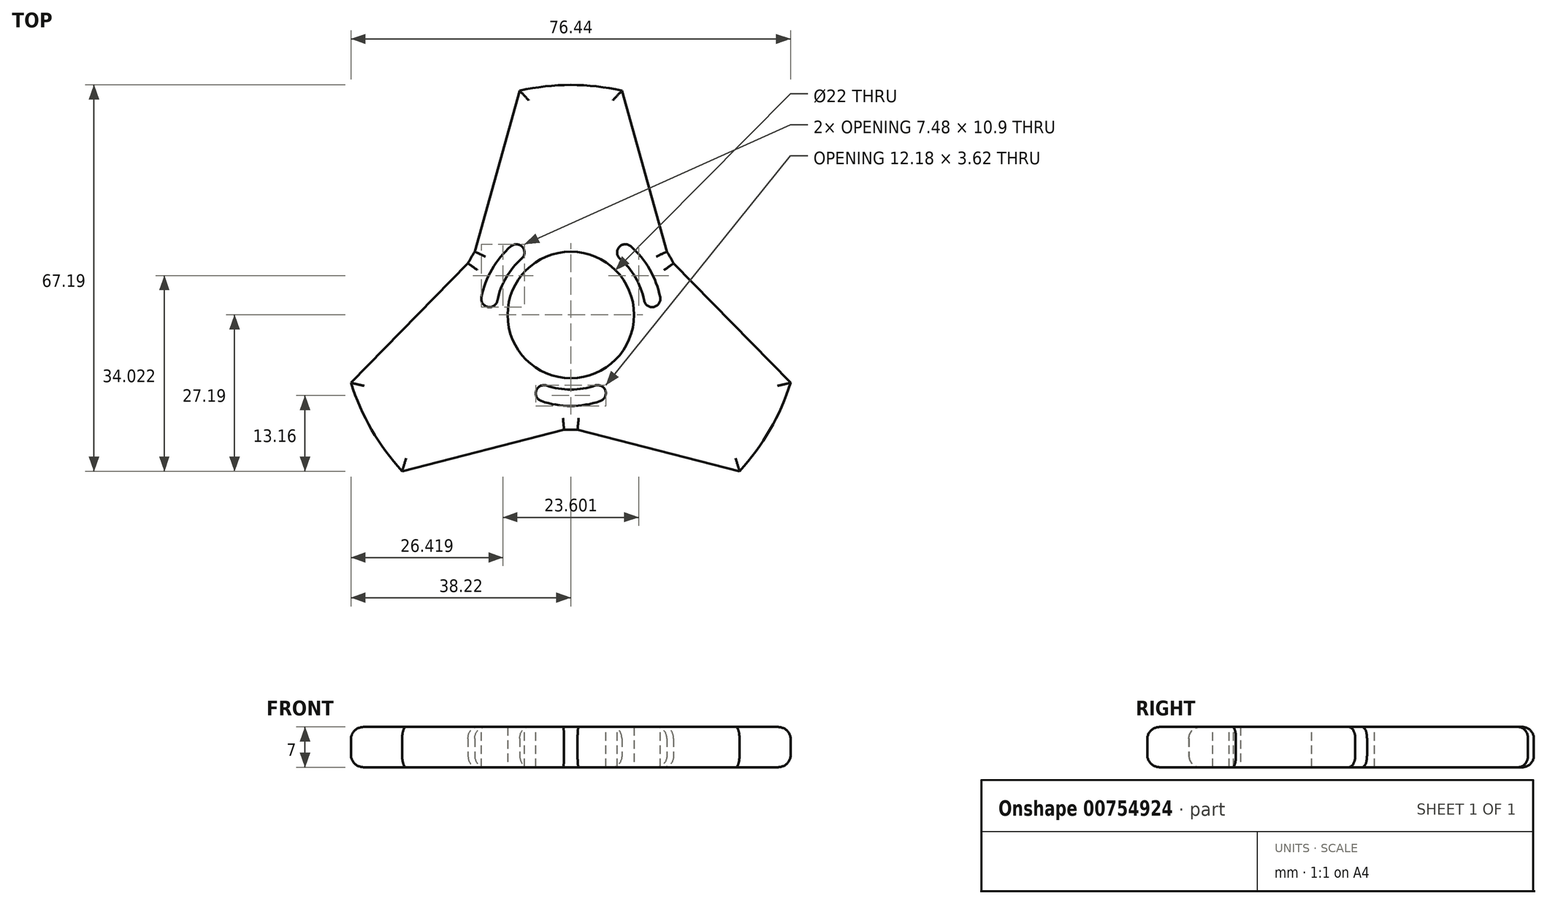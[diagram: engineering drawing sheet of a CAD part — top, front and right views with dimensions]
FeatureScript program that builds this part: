
annotation { "Feature Type Name" : "Feature", "Feature Type Description" : "" }
export const myFeature = defineFeature(function(context is Context, id is Id, definition is map)
    precondition{}
    {
        {
            var Q0;
            Q0=qCreatedBy(makeId("Top.planeOp"),FACE);
            var sketch = newSketch(context, id + "F0", { "sketchPlane" : qUnion([Q0])});
            skCircle(sketch, "E0", {"center": v(0, 0) * mm, "radius": 11 * mm});
            skLineSegment(sketch, "E1", {"start": v(0, 0) * mm, "end": v(0, 40) * mm, "construction": true});
            skLineSegment(sketch, "E2.1.0", {"start": v(0, 0) * mm, "end": v(-34.64, -20) * mm, "construction": true});
            skLineSegment(sketch, "E2.2.0", {"start": v(0, 0) * mm, "end": v(34.64, -20) * mm, "construction": true});
            skCircle(sketch, "E3", {"center": v(0, 0) * mm, "radius": 20 * mm, "construction": true});
            skCircle(sketch, "E4", {"center": v(0, 0) * mm, "radius": 40 * mm, "construction": true});
            skLineSegment(sketch, "E5", {"start": v(-72.61, 11) * mm, "end": v(59.89, 11) * mm, "construction": true});
            skLineSegment(sketch, "E6", {"start": v(-16.7, 11) * mm, "end": v(-8.88, 39) * mm});
            skLineSegment(sketch, "E7.MirrorCS", {"start": v(16.7, 11) * mm, "end": v(8.88, 39) * mm});
            skArc(sketch, "E8", {"start": v(-8.88, 39) * mm, "mid": v(0, 40) * mm, "end": v(8.88, 39) * mm});
            skArc(sketch, "E9.1.0", {"start": v(-29.33, -27.2) * mm, "mid": v(-34.64, -20) * mm, "end": v(-38.22, -11.8) * mm});
            skLineSegment(sketch, "E9.1.1", {"start": v(-1.17, -19.97) * mm, "end": v(-29.33, -27.2) * mm});
            skLineSegment(sketch, "E9.1.2", {"start": v(-17.88, 8.97) * mm, "end": v(-38.22, -11.8) * mm});
            skArc(sketch, "E9.2.0", {"start": v(38.22, -11.8) * mm, "mid": v(34.64, -20) * mm, "end": v(29.33, -27.2) * mm});
            skLineSegment(sketch, "E9.2.1", {"start": v(17.88, 8.97) * mm, "end": v(38.22, -11.8) * mm});
            skLineSegment(sketch, "E9.2.2", {"start": v(1.17, -19.97) * mm, "end": v(29.33, -27.2) * mm});
            skArc(sketch, "E10", {"start": v(-17.88, 8.97) * mm, "mid": v(-17.32, 10) * mm, "end": v(-16.7, 11) * mm});
            skArc(sketch, "E11", {"start": v(16.7, 11) * mm, "mid": v(17.32, 10) * mm, "end": v(17.88, 8.97) * mm});
            skArc(sketch, "E12", {"start": v(-1.17, -19.97) * mm, "mid": v(0, -20) * mm, "end": v(1.17, -19.97) * mm});
            skSolve(sketch);
        }
        {
            var Q0;
            Q0=makeQuery(id+"F0.imprint","IMPRINT",FACE,{"disambiguationData":[TD([[makeQuery(id+"F0.imprint","IMPRINT",EDGE,{"derivedFrom":sQuery(id+"F0.wireOp",EDGE,"E0")}),-1.0]])]});
            extrude(context, id + "F1", {"entities" : qUnion([Q0]), "depth" : 7 * mm, "offsetDistance" : 25 * mm});
        }
        {
            var Q0;
            Q0=makeQuery(id+"F1.opExtrude","CAP_FACE",FACE,{"disambiguationData":[OSD([sQuery(id+"F0.wireOp",EDGE,"E0"),sQuery(id+"F0.wireOp",EDGE,"E6"),sQuery(id+"F0.wireOp",EDGE,"E7.MirrorCS"),sQuery(id+"F0.wireOp",EDGE,"E8"),sQuery(id+"F0.wireOp",EDGE,"E9.1.0"),sQuery(id+"F0.wireOp",EDGE,"E9.1.1"),sQuery(id+"F0.wireOp",EDGE,"E9.1.2"),sQuery(id+"F0.wireOp",EDGE,"E9.2.0"),sQuery(id+"F0.wireOp",EDGE,"E9.2.1"),sQuery(id+"F0.wireOp",EDGE,"E9.2.2"),sQuery(id+"F0.wireOp",EDGE,"E10"),sQuery(id+"F0.wireOp",EDGE,"E11"),sQuery(id+"F0.wireOp",EDGE,"E12")])],"isStart":false});
            var sketch = newSketch(context, id + "F2", { "sketchPlane" : qUnion([Q0])});
            skCircle(sketch, "E13", {"center": v(0, 0) * mm, "radius": 13 * mm, "construction": true});
            skCircle(sketch, "E14", {"center": v(0, 0) * mm, "radius": 15.84 * mm, "construction": true});
            skCircle(sketch, "E15", {"center": v(0, 0) * mm, "radius": 14.42 * mm, "construction": true});
            skArc(sketch, "E16", {"start": v(-4.2, -12.3) * mm, "mid": v(-6.01, -13.18) * mm, "end": v(-5.13, -14.99) * mm});
            skLineSegment(sketch, "E17", {"start": v(0, 0) * mm, "end": v(0, -20) * mm, "construction": true});
            skArc(sketch, "E18.MirrorC", {"start": v(4.2, -12.3) * mm, "mid": v(6.01, -13.18) * mm, "end": v(5.13, -14.99) * mm});
            skArc(sketch, "E19", {"start": v(-4.2, -12.3) * mm, "mid": v(0, -13) * mm, "end": v(4.2, -12.3) * mm});
            skArc(sketch, "E20", {"start": v(-5.13, -14.99) * mm, "mid": v(0, -15.84) * mm, "end": v(5.13, -14.99) * mm});
            skArc(sketch, "E21.1.0", {"start": v(15.54, 3.05) * mm, "mid": v(13.72, 7.92) * mm, "end": v(10.41, 11.94) * mm});
            skArc(sketch, "E21.1.1", {"start": v(8.54, 9.8) * mm, "mid": v(8.4, 11.8) * mm, "end": v(10.41, 11.94) * mm});
            skArc(sketch, "E21.1.2", {"start": v(12.75, 2.5) * mm, "mid": v(11.25, 6.5) * mm, "end": v(8.54, 9.8) * mm});
            skArc(sketch, "E21.1.3", {"start": v(12.75, 2.5) * mm, "mid": v(14.42, 1.38) * mm, "end": v(15.54, 3.05) * mm});
            skArc(sketch, "E21.2.0", {"start": v(-10.41, 11.94) * mm, "mid": v(-13.72, 7.92) * mm, "end": v(-15.54, 3.05) * mm});
            skArc(sketch, "E21.2.1", {"start": v(-12.75, 2.5) * mm, "mid": v(-14.42, 1.38) * mm, "end": v(-15.54, 3.05) * mm});
            skArc(sketch, "E21.2.2", {"start": v(-8.54, 9.8) * mm, "mid": v(-11.25, 6.5) * mm, "end": v(-12.75, 2.5) * mm});
            skArc(sketch, "E21.2.3", {"start": v(-8.54, 9.8) * mm, "mid": v(-8.4, 11.8) * mm, "end": v(-10.41, 11.94) * mm});
            skSolve(sketch);
        }
        {
            var Q0;
            Q0 = qSketchRegion(id + "F2", true);
            extrude(context, id + "F3", {"entities" : qUnion([Q0]), "operationType" : NewBodyOperationType.REMOVE, "endBound" : BoundingType.THROUGH_ALL, "oppositeDirection" : true, "depth" : 25 * mm, "offsetDistance" : 25 * mm});
        }
        {
            var Q0;
            Q0=makeQuery(id+"F1.opExtrude","CAP_EDGE",EDGE,{"disambiguationData":[OSD([sQuery(id+"F0.wireOp",EDGE,"E7.MirrorCS")])],"isStart":false});
            var Q1;
            Q1=makeQuery(id+"F1.opExtrude","CAP_EDGE",EDGE,{"disambiguationData":[OSD([sQuery(id+"F0.wireOp",EDGE,"E9.2.1")])],"isStart":false});
            var Q2;
            Q2=makeQuery(id+"F1.opExtrude","CAP_EDGE",EDGE,{"disambiguationData":[OSD([sQuery(id+"F0.wireOp",EDGE,"E11")])],"isStart":false});
            var Q3;
            Q3=makeQuery(id+"F1.opExtrude","CAP_EDGE",EDGE,{"disambiguationData":[OSD([sQuery(id+"F0.wireOp",EDGE,"E9.2.0")])],"isStart":false});
            var Q4;
            Q4=makeQuery(id+"F1.opExtrude","CAP_EDGE",EDGE,{"disambiguationData":[OSD([sQuery(id+"F0.wireOp",EDGE,"E9.2.2")])],"isStart":false});
            var Q5;
            Q5=makeQuery(id+"F1.opExtrude","CAP_EDGE",EDGE,{"disambiguationData":[OSD([sQuery(id+"F0.wireOp",EDGE,"E12")])],"isStart":false});
            var Q6;
            Q6=makeQuery(id+"F1.opExtrude","CAP_EDGE",EDGE,{"disambiguationData":[OSD([sQuery(id+"F0.wireOp",EDGE,"E9.1.1")])],"isStart":false});
            var Q7;
            Q7=makeQuery(id+"F1.opExtrude","CAP_EDGE",EDGE,{"disambiguationData":[OSD([sQuery(id+"F0.wireOp",EDGE,"E9.1.0")])],"isStart":false});
            var Q8;
            Q8=makeQuery(id+"F1.opExtrude","CAP_EDGE",EDGE,{"disambiguationData":[OSD([sQuery(id+"F0.wireOp",EDGE,"E9.1.2")])],"isStart":false});
            var Q9;
            Q9=makeQuery(id+"F1.opExtrude","CAP_EDGE",EDGE,{"disambiguationData":[OSD([sQuery(id+"F0.wireOp",EDGE,"E10")])],"isStart":false});
            var Q10;
            Q10=makeQuery(id+"F1.opExtrude","CAP_EDGE",EDGE,{"disambiguationData":[OSD([sQuery(id+"F0.wireOp",EDGE,"E6")])],"isStart":false});
            var Q11;
            Q11=makeQuery(id+"F1.opExtrude","CAP_EDGE",EDGE,{"disambiguationData":[OSD([sQuery(id+"F0.wireOp",EDGE,"E8")])],"isStart":false});
            fillet(context, id + "F4", {"entities" : qUnion([Q0, Q1, Q2, Q3, Q4, Q5, Q6, Q7, Q8, Q9, Q10, Q11]), "radius" : 2 * mm, "tangentPropagation" : true, "allowEdgeOverflow" : false});
        }
        {
            var Q0;
            Q0=makeQuery(id+"F1.opExtrude","CAP_EDGE",EDGE,{"disambiguationData":[OSD([sQuery(id+"F0.wireOp",EDGE,"E9.1.1")])],"isStart":true});
            var Q1;
            Q1=makeQuery(id+"F1.opExtrude","CAP_EDGE",EDGE,{"disambiguationData":[OSD([sQuery(id+"F0.wireOp",EDGE,"E12")])],"isStart":true});
            var Q2;
            Q2=makeQuery(id+"F1.opExtrude","CAP_EDGE",EDGE,{"disambiguationData":[OSD([sQuery(id+"F0.wireOp",EDGE,"E9.2.2")])],"isStart":true});
            var Q3;
            Q3=makeQuery(id+"F1.opExtrude","CAP_EDGE",EDGE,{"disambiguationData":[OSD([sQuery(id+"F0.wireOp",EDGE,"E9.2.0")])],"isStart":true});
            var Q4;
            Q4=makeQuery(id+"F1.opExtrude","CAP_EDGE",EDGE,{"disambiguationData":[OSD([sQuery(id+"F0.wireOp",EDGE,"E9.2.1")])],"isStart":true});
            var Q5;
            Q5=makeQuery(id+"F1.opExtrude","CAP_EDGE",EDGE,{"disambiguationData":[OSD([sQuery(id+"F0.wireOp",EDGE,"E11")])],"isStart":true});
            var Q6;
            Q6=makeQuery(id+"F1.opExtrude","CAP_EDGE",EDGE,{"disambiguationData":[OSD([sQuery(id+"F0.wireOp",EDGE,"E7.MirrorCS")])],"isStart":true});
            var Q7;
            Q7=makeQuery(id+"F1.opExtrude","CAP_EDGE",EDGE,{"disambiguationData":[OSD([sQuery(id+"F0.wireOp",EDGE,"E8")])],"isStart":true});
            var Q8;
            Q8=makeQuery(id+"F1.opExtrude","CAP_EDGE",EDGE,{"disambiguationData":[OSD([sQuery(id+"F0.wireOp",EDGE,"E6")])],"isStart":true});
            var Q9;
            Q9=makeQuery(id+"F1.opExtrude","CAP_EDGE",EDGE,{"disambiguationData":[OSD([sQuery(id+"F0.wireOp",EDGE,"E10")])],"isStart":true});
            var Q10;
            Q10=makeQuery(id+"F1.opExtrude","CAP_EDGE",EDGE,{"disambiguationData":[OSD([sQuery(id+"F0.wireOp",EDGE,"E9.1.2")])],"isStart":true});
            var Q11;
            Q11=makeQuery(id+"F1.opExtrude","CAP_EDGE",EDGE,{"disambiguationData":[OSD([sQuery(id+"F0.wireOp",EDGE,"E9.1.0")])],"isStart":true});
            fillet(context, id + "F5", {"entities" : qUnion([Q0, Q1, Q2, Q3, Q4, Q5, Q6, Q7, Q8, Q9, Q10, Q11]), "radius" : 2 * mm, "tangentPropagation" : true, "allowEdgeOverflow" : false});
        }
    });
